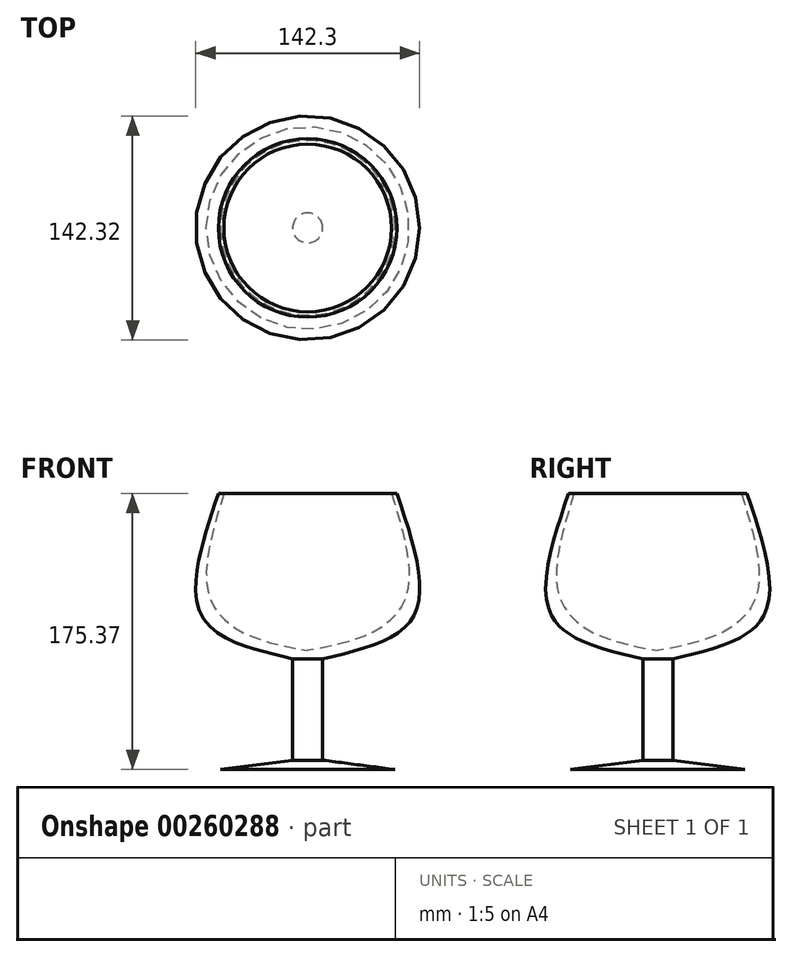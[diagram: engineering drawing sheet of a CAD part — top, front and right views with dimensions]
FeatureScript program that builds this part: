
annotation { "Feature Type Name" : "Feature", "Feature Type Description" : "" }
export const myFeature = defineFeature(function(context is Context, id is Id, definition is map)
    precondition{}
    {
        {
            var Q0;
            Q0=qCreatedBy(makeId("Front.planeOp"),FACE);
            var sketch = newSketch(context, id + "F0", { "sketchPlane" : qUnion([Q0])});
            skLineSegment(sketch, "E0", {"start": v(0, 98.3) * mm, "end": v(0, -104.9) * mm});
            skLineSegment(sketch, "E1", {"start": v(0, -104.9) * mm, "end": v(-55.37, -105.35) * mm});
            skLineSegment(sketch, "E2", {"start": v(-55.37, -105.35) * mm, "end": v(-9.54, -99.37) * mm});
            skLineSegment(sketch, "E3", {"start": v(-9.54, -99.37) * mm, "end": v(-9.54, -34.94) * mm});
            skFitSpline(sketch, "E4", {"points": [v(-56.7, 70.02) * mm, v(-67.33, -7.7) * mm, v(-9.54, -34.94) * mm], "startDerivative": vector(-57.55, -171.64) * mm, "endDerivative": vector(155.53, -35.96) * mm});
            skLineSegment(sketch, "E5", {"start": v(-56.7, 70.02) * mm, "end": v(-53.24, 70.02) * mm});
            skFitSpline(sketch, "E6", {"points": [v(-53.24, 70.02) * mm, v(-63.46, 8.27) * mm, v(-41.97, -17.8) * mm, v(0, -29.77) * mm], "startDerivative": vector(-53.17, -175.3) * mm, "endDerivative": vector(138.25, -25.66) * mm});
            skSolve(sketch);
        }
        {
            var Q0;
            {var subQ0=sQuery(id+"F0.wireOp",EDGE,"E1");Q0=makeQuery(id+"F0.imprint","IMPRINT",FACE,{"disambiguationData":[TD([[makeQuery(id+"F0.imprint","IMPRINT",EDGE,{"derivedFrom":subQ0}),-1.0]])]});}
            var Q1;
            Q1=sQuery(id+"F0.wireOp",EDGE,"E0");
            revolve(context, id + "F1", {"entities" : qUnion([Q0]), "axis" : qUnion([Q1]), "revolveType" : RevolveType.FULL});
        }
    });
